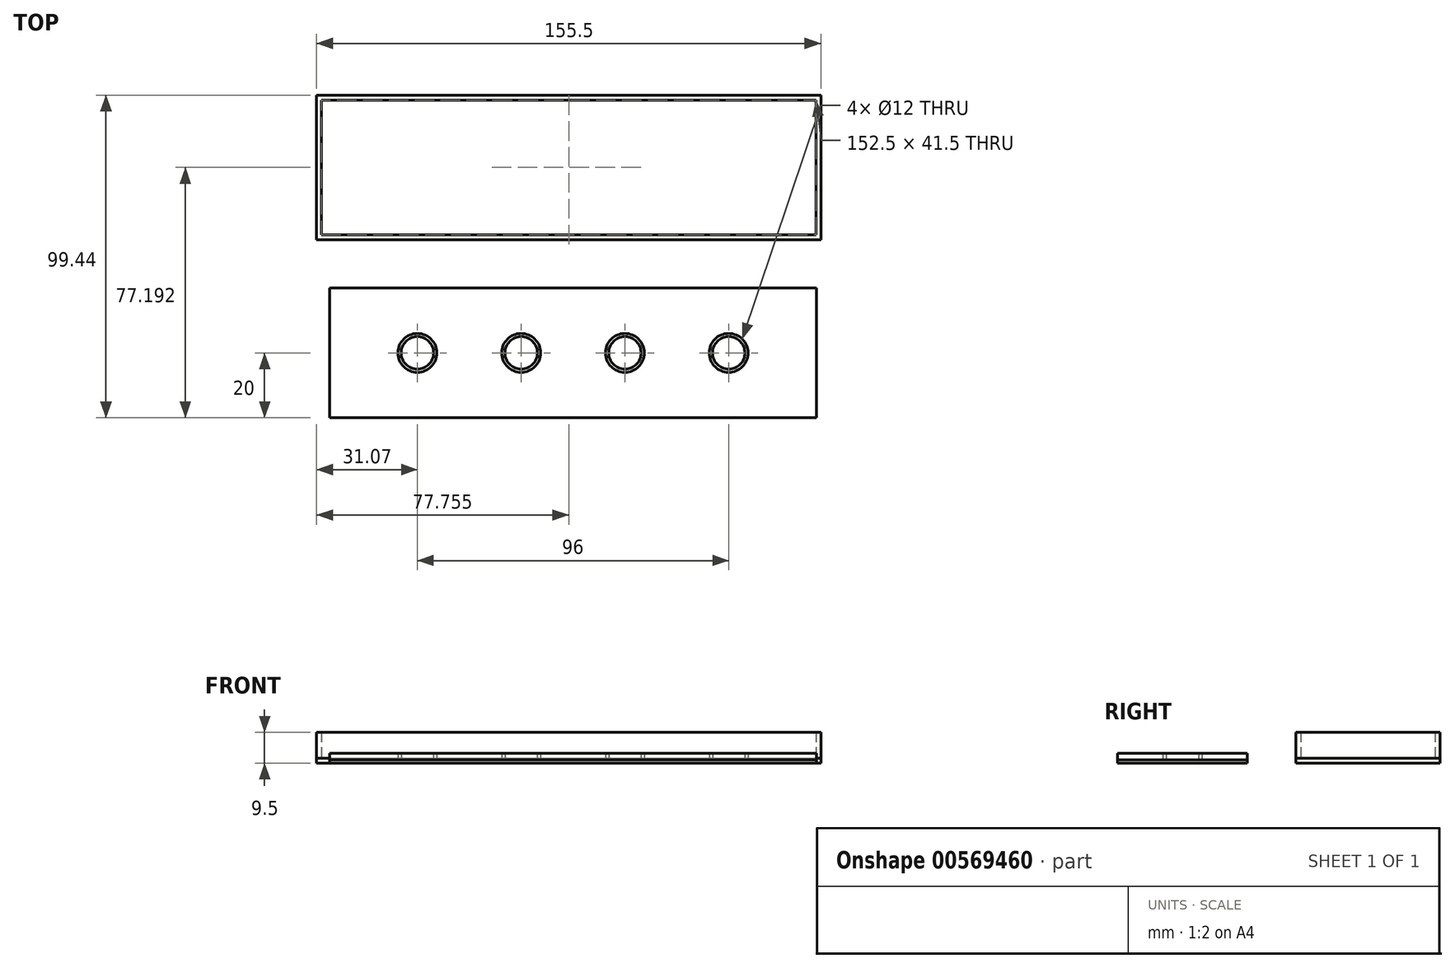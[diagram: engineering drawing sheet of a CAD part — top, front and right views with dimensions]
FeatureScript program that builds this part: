
annotation { "Feature Type Name" : "Feature", "Feature Type Description" : "" }
export const myFeature = defineFeature(function(context is Context, id is Id, definition is map)
    precondition{}
    {
        {
            var Q0;
            Q0=qCreatedBy(makeId("Top.planeOp"),FACE);
            var sketch = newSketch(context, id + "F0", { "sketchPlane" : qUnion([Q0])});
            skCircle(sketch, "E0", {"center": v(0, 0) * mm, "radius": 5 * mm});
            skCircle(sketch, "E1", {"center": v(0, 0) * mm, "radius": 6 * mm});
            skCircle(sketch, "E2.1.0.0", {"center": v(32, 0) * mm, "radius": 5 * mm});
            skCircle(sketch, "E2.1.0.1", {"center": v(32, 0) * mm, "radius": 6 * mm});
            skCircle(sketch, "E2.2.0.0", {"center": v(64, 0) * mm, "radius": 5 * mm});
            skCircle(sketch, "E2.2.0.1", {"center": v(64, 0) * mm, "radius": 6 * mm});
            skCircle(sketch, "E2.3.0.0", {"center": v(96, 0) * mm, "radius": 5 * mm});
            skCircle(sketch, "E2.3.0.1", {"center": v(96, 0) * mm, "radius": 6 * mm});
            skLineSegment(sketch, "E2.direction1", {"start": v(0, 0) * mm, "end": v(32, 0) * mm, "construction": true});
            skLineSegment(sketch, "E3.bottom", {"start": v(-27, -20) * mm, "end": v(123, -20) * mm});
            skLineSegment(sketch, "E3.top", {"start": v(-27, 20) * mm, "end": v(123, 20) * mm});
            skLineSegment(sketch, "E3.left", {"start": v(-27, -20) * mm, "end": v(-27, 20) * mm});
            skLineSegment(sketch, "E3.right", {"start": v(123, -20) * mm, "end": v(123, 20) * mm});
            skSolve(sketch);
        }
        {
            var Q0;
            Q0=makeQuery(id+"F0.imprint","IMPRINT",FACE,{"disambiguationData":[TD([[makeQuery(id+"F0.imprint","IMPRINT",EDGE,{"derivedFrom":sQuery(id+"F0.wireOp",EDGE,"E1")}),-1.0]])]});
            var Q1;
            Q1=makeQuery(id+"F2.opExtrude","CAP_FACE",FACE,{"disambiguationData":[OSD([sQuery(id+"F0.wireOp",EDGE,"E1"),sQuery(id+"F0.wireOp",EDGE,"E2.1.0.1"),sQuery(id+"F0.wireOp",EDGE,"E2.2.0.1"),sQuery(id+"F0.wireOp",EDGE,"E2.3.0.1"),sQuery(id+"F0.wireOp",EDGE,"E3.bottom"),sQuery(id+"F0.wireOp",EDGE,"E3.top"),sQuery(id+"F0.wireOp",EDGE,"E3.left"),sQuery(id+"F0.wireOp",EDGE,"E3.right")])],"isStart":false});
            var Q2;
            Q2=makeQuery(id+"F2.opExtrude","CAP_FACE",FACE,{"disambiguationData":[OSD([sQuery(id+"F0.wireOp",EDGE,"E2.1.0.0")])],"isStart":false});
            var Q3;
            Q3=makeQuery(id+"F2.opExtrude","CAP_FACE",FACE,{"disambiguationData":[OSD([sQuery(id+"F0.wireOp",EDGE,"E2.2.0.0")])],"isStart":false});
            var Q4;
            Q4=makeQuery(id+"F2.opExtrude","CAP_FACE",FACE,{"disambiguationData":[OSD([sQuery(id+"F0.wireOp",EDGE,"E2.3.0.0")])],"isStart":false});
            var Q5;
            Q5=makeQuery(id+"F2.opExtrude","SWEPT_FACE",FACE,{"disambiguationData":[OSD([sQuery(id+"F0.wireOp",EDGE,"E3.bottom")])]});
            var Q6;
            Q6=makeQuery(id+"F2.opExtrude","SWEPT_FACE",FACE,{"disambiguationData":[OSD([sQuery(id+"F0.wireOp",EDGE,"E3.right")])]});
            var Q7;
            Q7=makeQuery(id+"F2.opExtrude","SWEPT_FACE",FACE,{"disambiguationData":[OSD([sQuery(id+"F0.wireOp",EDGE,"E3.top")])]});
            var Q8;
            Q8=makeQuery(id+"F2.opExtrude","SWEPT_FACE",FACE,{"disambiguationData":[OSD([sQuery(id+"F0.wireOp",EDGE,"E3.left")])]});
            var Q9;
            Q9=makeQuery(id+"F2.opExtrude","CAP_FACE",FACE,{"disambiguationData":[OSD([sQuery(id+"F0.wireOp",EDGE,"E1"),sQuery(id+"F0.wireOp",EDGE,"E2.1.0.1"),sQuery(id+"F0.wireOp",EDGE,"E2.2.0.1"),sQuery(id+"F0.wireOp",EDGE,"E2.3.0.1"),sQuery(id+"F0.wireOp",EDGE,"E3.bottom"),sQuery(id+"F0.wireOp",EDGE,"E3.top"),sQuery(id+"F0.wireOp",EDGE,"E3.left"),sQuery(id+"F0.wireOp",EDGE,"E3.right")])],"isStart":true});
            var Q10;
            Q10=makeQuery(id+"F2.opExtrude","CAP_FACE",FACE,{"disambiguationData":[OSD([sQuery(id+"F0.wireOp",EDGE,"E0")])],"isStart":false});
            var Q11;
            Q11=makeQuery(id+"F2.opExtrude","CAP_FACE",FACE,{"disambiguationData":[OSD([sQuery(id+"F0.wireOp",EDGE,"E2.1.0.0")])],"isStart":true});
            var Q12;
            Q12=makeQuery(id+"F2.opExtrude","CAP_FACE",FACE,{"disambiguationData":[OSD([sQuery(id+"F0.wireOp",EDGE,"E2.2.0.0")])],"isStart":true});
            var Q13;
            Q13=makeQuery(id+"F2.opExtrude","CAP_FACE",FACE,{"disambiguationData":[OSD([sQuery(id+"F0.wireOp",EDGE,"E2.3.0.0")])],"isStart":true});
            var Q14;
            Q14=makeQuery(id+"F0.imprint","IMPRINT",FACE,{"disambiguationData":[TD([[makeQuery(id+"F0.imprint","IMPRINT",EDGE,{"derivedFrom":sQuery(id+"F0.wireOp",EDGE,"E2.3.0.0")}),1.0]])]});
            var Q15;
            Q15=makeQuery(id+"F0.imprint","IMPRINT",FACE,{"disambiguationData":[TD([[makeQuery(id+"F0.imprint","IMPRINT",EDGE,{"derivedFrom":sQuery(id+"F0.wireOp",EDGE,"E2.1.0.0")}),1.0]])]});
            var Q16;
            Q16=makeQuery(id+"F0.imprint","IMPRINT",FACE,{"disambiguationData":[TD([[makeQuery(id+"F0.imprint","IMPRINT",EDGE,{"derivedFrom":sQuery(id+"F0.wireOp",EDGE,"E2.2.0.0")}),1.0]])]});
            var Q17;
            Q17=makeQuery(id+"F0.imprint","IMPRINT",FACE,{"disambiguationData":[TD([[makeQuery(id+"F0.imprint","IMPRINT",EDGE,{"derivedFrom":sQuery(id+"F0.wireOp",EDGE,"E2.1.0.0")}),-1.0]])]});
            var Q18;
            Q18=makeQuery(id+"F0.imprint","IMPRINT",FACE,{"disambiguationData":[TD([[makeQuery(id+"F0.imprint","IMPRINT",EDGE,{"derivedFrom":sQuery(id+"F0.wireOp",EDGE,"E2.2.0.0")}),-1.0]])]});
            var Q19;
            Q19=makeQuery(id+"F0.imprint","IMPRINT",FACE,{"disambiguationData":[TD([[makeQuery(id+"F0.imprint","IMPRINT",EDGE,{"derivedFrom":sQuery(id+"F0.wireOp",EDGE,"E0")}),-1.0]])]});
            var Q20;
            Q20=makeQuery(id+"F2.opExtrude","CAP_FACE",FACE,{"disambiguationData":[OSD([sQuery(id+"F0.wireOp",EDGE,"E0")])],"isStart":true});
            var Q21;
            Q21=makeQuery(id+"F0.imprint","IMPRINT",FACE,{"disambiguationData":[TD([[makeQuery(id+"F0.imprint","IMPRINT",EDGE,{"derivedFrom":sQuery(id+"F0.wireOp",EDGE,"E2.3.0.0")}),-1.0]])]});
            var Q22;
            Q22=makeQuery(id+"F0.imprint","IMPRINT",FACE,{"disambiguationData":[TD([[makeQuery(id+"F0.imprint","IMPRINT",EDGE,{"derivedFrom":sQuery(id+"F0.wireOp",EDGE,"E0")}),1.0]])]});
            extrude(context, id + "F1", {"entities" : qUnion([Q0, Q1, Q2, Q3, Q4, Q5, Q6, Q7, Q8, Q9, Q10, Q11, Q12, Q13, Q14, Q15, Q16, Q17, Q18, Q19, Q20, Q21, Q22]), "depth" : 1 * mm, "offsetDistance" : 25 * mm});
        }
        {
            var Q0;
            Q0=makeQuery(id+"F0.imprint","IMPRINT",FACE,{"disambiguationData":[TD([[makeQuery(id+"F0.imprint","IMPRINT",EDGE,{"derivedFrom":sQuery(id+"F0.wireOp",EDGE,"E2.5.0.0")}),1.0]])]});
            var Q1;
            Q1=makeQuery(id+"F0.imprint","IMPRINT",FACE,{"disambiguationData":[TD([[makeQuery(id+"F0.imprint","IMPRINT",EDGE,{"derivedFrom":sQuery(id+"F0.wireOp",EDGE,"E2.4.0.0")}),1.0]])]});
            var Q2;
            Q2=makeQuery(id+"F0.imprint","IMPRINT",FACE,{"disambiguationData":[TD([[makeQuery(id+"F0.imprint","IMPRINT",EDGE,{"derivedFrom":sQuery(id+"F0.wireOp",EDGE,"E2.3.0.0")}),1.0]])]});
            var Q3;
            Q3=makeQuery(id+"F0.imprint","IMPRINT",FACE,{"disambiguationData":[TD([[makeQuery(id+"F0.imprint","IMPRINT",EDGE,{"derivedFrom":sQuery(id+"F0.wireOp",EDGE,"E2.2.0.0")}),1.0]])]});
            var Q4;
            Q4=makeQuery(id+"F0.imprint","IMPRINT",FACE,{"disambiguationData":[TD([[makeQuery(id+"F0.imprint","IMPRINT",EDGE,{"derivedFrom":sQuery(id+"F0.wireOp",EDGE,"E1")}),-1.0]])]});
            var Q5;
            Q5=makeQuery(id+"F0.imprint","IMPRINT",FACE,{"disambiguationData":[TD([[makeQuery(id+"F0.imprint","IMPRINT",EDGE,{"derivedFrom":sQuery(id+"F0.wireOp",EDGE,"E2.1.0.0")}),1.0]])]});
            var Q6;
            Q6=makeQuery(id+"F0.imprint","IMPRINT",FACE,{"disambiguationData":[TD([[makeQuery(id+"F0.imprint","IMPRINT",EDGE,{"derivedFrom":sQuery(id+"F0.wireOp",EDGE,"E0")}),1.0]])]});
            var Q7;
            Q7=sQuery(id+"F0.wireOp",EDGE,"E0");
            var Q8;
            Q8=sQuery(id+"F0.wireOp",EDGE,"E2.1.0.0");
            extrude(context, id + "F2", {"entities" : qUnion([Q0, Q1, Q2, Q3, Q4, Q5, Q6]), "surfaceEntities" : qUnion([Q7, Q8]), "depth" : 3 * mm, "offsetDistance" : 25 * mm, "hasSecondDirection" : true, "secondDirectionOppositeDirection" : false, "secondDirectionDepth" : 1 * mm});
        }
        {
            var Q0;
            Q0=qCreatedBy(makeId("Top.planeOp"),FACE);
            var sketch = newSketch(context, id + "F3", { "sketchPlane" : qUnion([Q0])});
            skLineSegment(sketch, "E4.bottom", {"start": v(-29.57, 36.44) * mm, "end": v(122.93, 36.44) * mm});
            skLineSegment(sketch, "E4.top", {"start": v(-29.57, 77.94) * mm, "end": v(122.93, 77.94) * mm});
            skLineSegment(sketch, "E4.left", {"start": v(-29.57, 36.44) * mm, "end": v(-29.57, 77.94) * mm});
            skLineSegment(sketch, "E4.right", {"start": v(122.93, 36.44) * mm, "end": v(122.93, 77.94) * mm});
            skLineSegment(sketch, "E5.bottom", {"start": v(-31.07, 34.94) * mm, "end": v(124.43, 34.94) * mm});
            skLineSegment(sketch, "E5.top", {"start": v(-31.07, 79.44) * mm, "end": v(124.43, 79.44) * mm});
            skLineSegment(sketch, "E5.left", {"start": v(-31.07, 34.94) * mm, "end": v(-31.07, 79.44) * mm});
            skLineSegment(sketch, "E5.right", {"start": v(124.43, 34.94) * mm, "end": v(124.43, 79.44) * mm});
            skSolve(sketch);
        }
        {
            var Q0;
            Q0 = qSketchRegion(id + "F3", true);
            var Q1;
            Q1=makeQuery(id+"F3.imprint","IMPRINT",FACE,{"disambiguationData":[TD([[makeQuery(id+"F3.imprint","IMPRINT",EDGE,{"derivedFrom":sQuery(id+"F3.wireOp",EDGE,"E4.bottom")}),1.0]])]});
            extrude(context, id + "F4", {"entities" : qUnion([Q0, Q1]), "depth" : 1.5 * mm, "offsetDistance" : 25 * mm});
        }
        {
            var Q0;
            Q0=makeQuery(id+"F3.imprint","IMPRINT",FACE,{"disambiguationData":[TD([[makeQuery(id+"F3.imprint","IMPRINT",EDGE,{"derivedFrom":sQuery(id+"F3.wireOp",EDGE,"E4.bottom")}),-1.0]])]});
            extrude(context, id + "F5", {"entities" : qUnion([Q0]), "depth" : 9.5 * mm, "offsetDistance" : 25 * mm, "hasSecondDirection" : true, "secondDirectionOppositeDirection" : false, "secondDirectionDepth" : 1.5 * mm});
        }
    });
